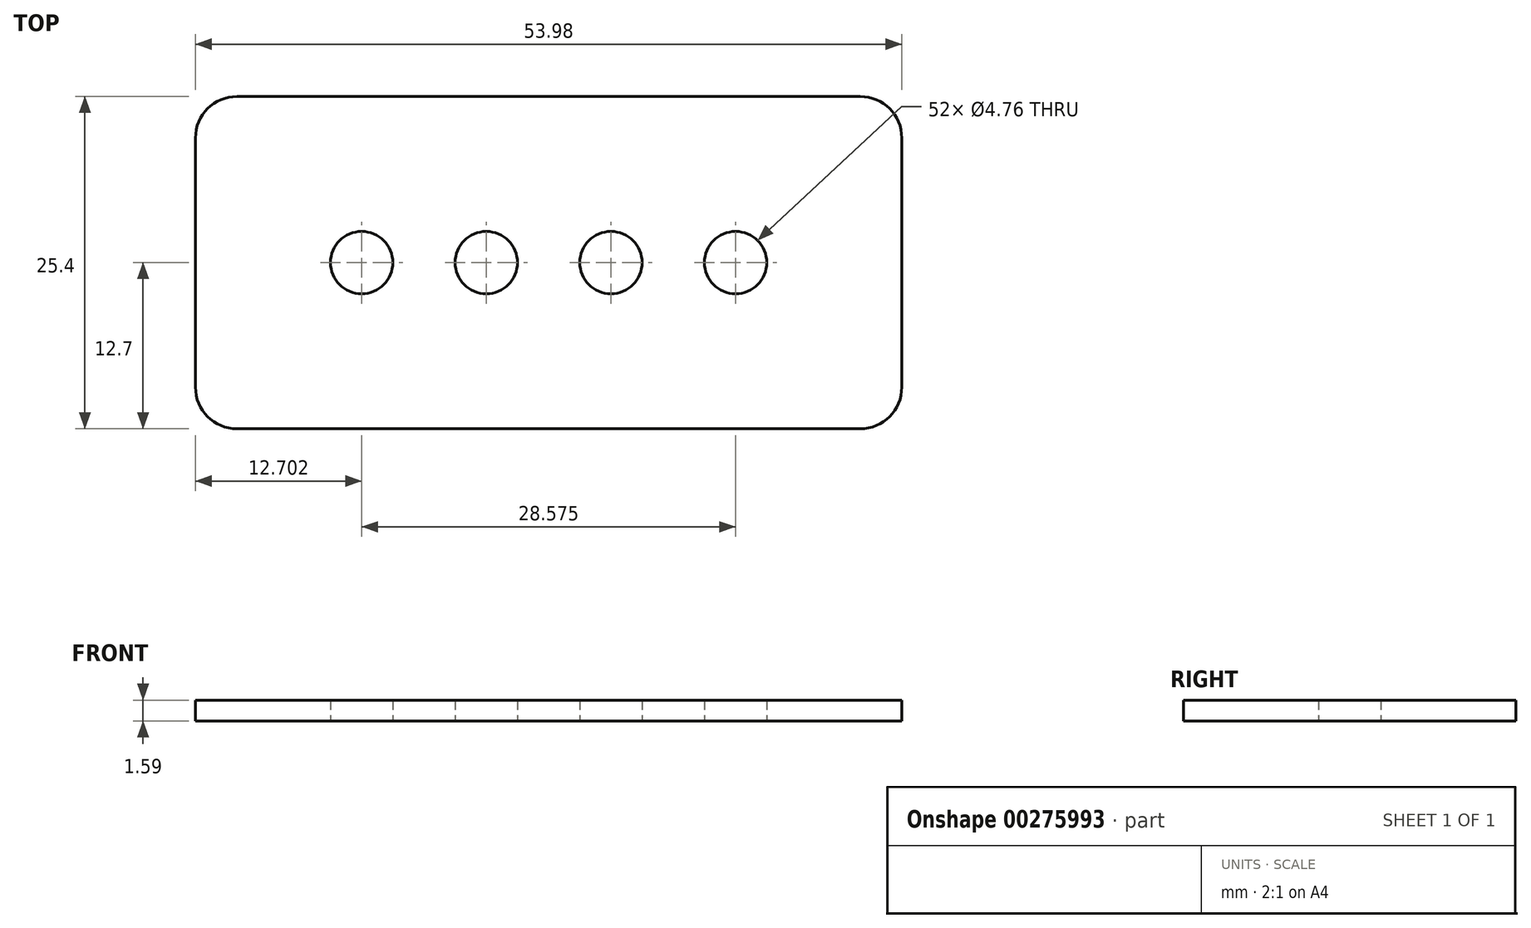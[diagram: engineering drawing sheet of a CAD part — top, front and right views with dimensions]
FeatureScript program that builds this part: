
annotation { "Feature Type Name" : "Feature", "Feature Type Description" : "" }
export const myFeature = defineFeature(function(context is Context, id is Id, definition is map)
    precondition{}
    {
        {
            var Q0;
            Q0=qCreatedBy(makeId("Top.planeOp"),FACE);
            var sketch = newSketch(context, id + "F0", { "sketchPlane" : qUnion([Q0])});
            skLineSegment(sketch, "E0.bottom", {"start": v(23.81, 12.7) * mm, "end": v(-23.81, 12.7) * mm});
            skLineSegment(sketch, "E0.top", {"start": v(23.81, -12.7) * mm, "end": v(-23.81, -12.7) * mm});
            skLineSegment(sketch, "E0.left", {"start": v(26.99, 9.53) * mm, "end": v(26.99, -9.53) * mm});
            skLineSegment(sketch, "E0.right", {"start": v(-26.99, 9.53) * mm, "end": v(-26.99, -9.53) * mm});
            skPoint(sketch, "E0.middle", {"position": v(0, 0) * mm});
            skCircle(sketch, "E1", {"center": v(4.76, 0) * mm, "radius": 2.38 * mm});
            skCircle(sketch, "E2", {"center": v(14.29, 0) * mm, "radius": 2.38 * mm});
            skCircle(sketch, "E3.MirrorC", {"center": v(-4.76, 0) * mm, "radius": 2.38 * mm});
            skCircle(sketch, "E4.MirrorC", {"center": v(-14.29, 0) * mm, "radius": 2.38 * mm});
            skPoint(sketch, "E5.visualSharp", {"position": v(-26.99, 12.7) * mm});
            skArc(sketch, "E5.filletArc", {"start": v(-23.81, 12.7) * mm, "mid": v(-26.06, 11.77) * mm, "end": v(-26.99, 9.53) * mm});
            skPoint(sketch, "E6.visualSharp", {"position": v(26.99, 12.7) * mm});
            skArc(sketch, "E6.filletArc", {"start": v(26.99, 9.53) * mm, "mid": v(26.06, 11.77) * mm, "end": v(23.81, 12.7) * mm});
            skPoint(sketch, "E7.visualSharp", {"position": v(26.99, -12.7) * mm});
            skArc(sketch, "E7.filletArc", {"start": v(23.81, -12.7) * mm, "mid": v(26.06, -11.77) * mm, "end": v(26.99, -9.53) * mm});
            skPoint(sketch, "E8.visualSharp", {"position": v(-26.99, -12.7) * mm});
            skArc(sketch, "E8.filletArc", {"start": v(-26.99, -9.53) * mm, "mid": v(-26.06, -11.77) * mm, "end": v(-23.81, -12.7) * mm});
            skSolve(sketch);
        }
        {
            var Q0;
            Q0 = qSketchRegion(id + "F0", true);
            extrude(context, id + "F1", {"entities" : qUnion([Q0]), "depth" : 1.59 * mm});
        }
    });
